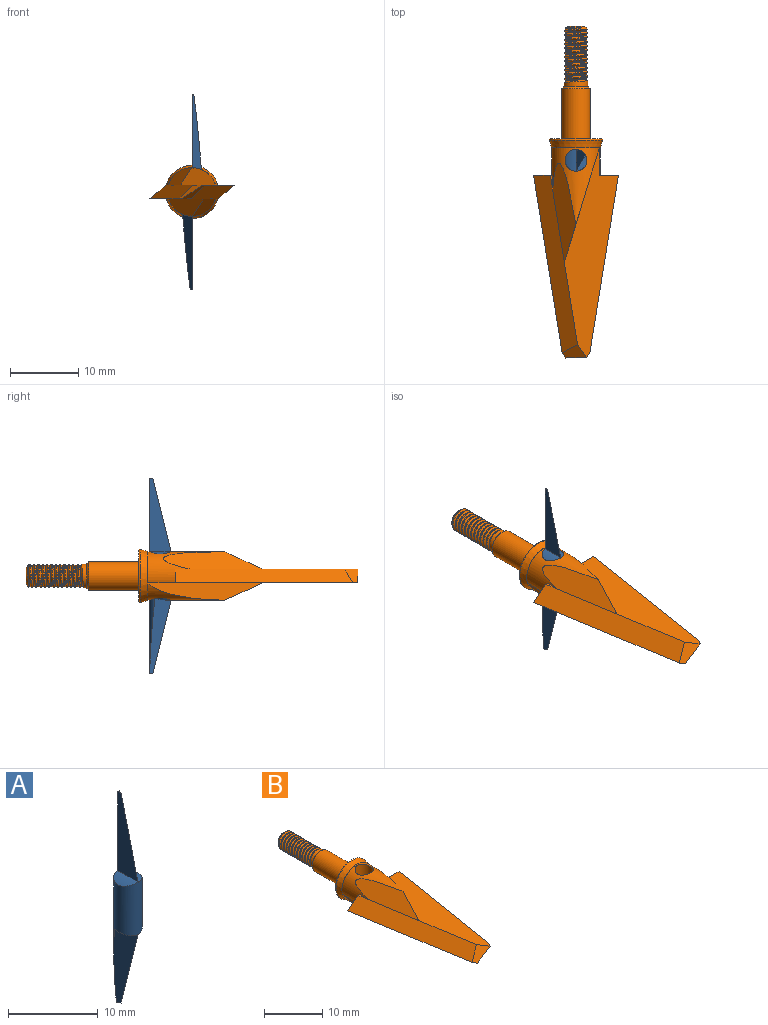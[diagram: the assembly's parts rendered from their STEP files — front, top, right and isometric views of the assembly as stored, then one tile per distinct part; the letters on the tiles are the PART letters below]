
ASSEMBLY  parts=2 mates=1
PART A: 13 faces, bbox 3.3x3.3x28.7 mm
  f0: cylinder r=1.59mm len=28.58mm, axis (0,0,-1), area 87.8mm2, adj f1,f2,f3,f4,f6,f7,f8,f9
  f1: cylinder r=3.56mm len=2.38mm, axis (0,1,0), area 1.6mm2, adj f0,f5,f9,f12
  f2: plane 10.73x3.18mm, normal (-1,0,0), area 19.8mm2, adj f0,f4,f7,f11
  f3: cylinder r=3.56mm len=3.18mm, axis (0,1,0), area 4.1mm2, adj f0,f6
  f4: plane 11.09x3.24mm, normal (0.87,-0.49,0.12), area 19.3mm2, adj f0,f2,f8,f11
  f5: plane 0.07x0.04mm, normal (-0.5,0.86,0.12), area 0mm2, adj f1,f9,f12
  f6: plane 10.73x3.18mm, normal (1,0,0), area 19.8mm2, adj f0,f3,f9,f10
  f7: cylinder r=3.56mm len=3.18mm, axis (0,1,0), area 4.1mm2, adj f0,f2
  f8: cylinder r=3.56mm len=2.38mm, axis (0,1,0), area 1.6mm2, adj f0,f4
  f9: plane 11.03x3.17mm, normal (-0.87,-0.49,-0.12), area 19.3mm2, adj f0,f1,f5,f6,f10,f12
  f10: plane 0.51x0.27mm, normal (0,0,-1), area 0.1mm2, adj f0,f6,f9
  f11: plane 0.51x0.27mm, normal (0,0,1), area 0.1mm2, adj f0,f2,f4
  f12: plane 1.08x0.59mm, normal (0.08,0.11,-0.99), area 0.1mm2, adj f1,f5,f9
PART B: 44 faces, bbox 12.4x48.5x8.4 mm
  f0: cylinder r=2.08mm len=7.37mm, axis (0,-1,0), area 96.4mm2, adj f2,f36
  f1: plane 3.66x3.66mm, normal (0,1,0), area 0.9mm2, adj f2,f3
  f2: cone r=1.83mm half-angle=45deg, axis (0,-1,0), area 4.4mm2, adj f0,f1
  f3: cylinder r=1.75mm len=3.51mm, axis (0,-1,0), area 7.4mm2, adj f1,f4,f18,f19,f21
  f4: cylinder r=1.75mm len=3.51mm, axis (0,-1,0), area 1mm2, adj f3,f5,f19,f21
  f5: cylinder r=1.75mm len=3.51mm, axis (0,-1,0), area 1mm2, adj f4,f6,f19,f21
  f6: cylinder r=1.75mm len=3.51mm, axis (0,-1,0), area 1mm2, adj f5,f7,f19,f21
  f7: cylinder r=1.75mm len=3.51mm, axis (0,-1,0), area 1mm2, adj f6,f8,f19,f21
  f8: cylinder r=1.75mm len=3.51mm, axis (0,-1,0), area 1mm2, adj f7,f9,f19,f21
  f9: cylinder r=1.75mm len=3.51mm, axis (0,-1,0), area 1mm2, adj f8,f10,f19,f21
  f10: cylinder r=1.75mm len=3.51mm, axis (0,-1,0), area 1mm2, adj f9,f11,f19,f21
  f11: cylinder r=1.75mm len=3.51mm, axis (0,-1,0), area 1mm2, adj f10,f12,f19,f21
  f12: cylinder r=1.75mm len=3.51mm, axis (0,-1,0), area 1mm2, adj f11,f13,f19,f21
  f13: cylinder r=1.75mm len=3.51mm, axis (0,-1,0), area 1mm2, adj f12,f14,f19,f21
  f14: cylinder r=1.75mm len=3.51mm, axis (0,-1,0), area 1mm2, adj f13,f15,f19,f21
  f15: cylinder r=1.75mm len=1.33mm, axis (0,-1,0), area 0.1mm2, adj f14,f17,f21
  f16: plane 2.49x2.49mm, normal (0,1,0), area 4.9mm2, adj f17
  f17: cone r=1.24mm half-angle=45deg, axis (0,-1,0), area 4.6mm2, adj f15,f16,f19,f20,f21
  f18: plane 0.55x0.27mm, normal (0,0,-1), area 0.1mm2, adj f3,f19,f20,f21
  f19: bspline ~8.47x4.05mm, area 45.1mm2, adj f3,f4,f5,f6,f7,f8,f9,f10
  f20: cylinder r=1.48mm len=8.16mm, axis (0,1,0), area 20.7mm2, adj f17,f18,f19,f21
  f21: bspline ~8.23x4.05mm, area 41.3mm2, adj f3,f4,f5,f6,f7,f8,f9,f10
  f22: cylinder r=3.56mm len=11.24mm, axis (0,1,0), area 42.9mm2, adj f23,f24,f25,f26,f27,f37,f39
  f23: plane 16.75x5.11mm, normal (0.96,-0.29,0), area 29.3mm2, adj f22,f24,f28
  f24: plane 14.43x3.39mm, normal (-0.7,-0.11,0.71), area 37.1mm2, adj f22,f23,f34
  f25: plane 2.13x0.34mm, normal (0,0,1), area 0.4mm2, adj f22,f26,f34
  f26: plane 2.8x2.03mm, normal (0,1,0), area 3mm2, adj f22,f25,f27,f34
  f27: plane 30.73x7.91mm, normal (0,0,-1), area 114.7mm2, adj f22,f26,f30,f32,f33,f34,f41,f42
  f28: plane 30.73x7.91mm, normal (0,0,1), area 114.7mm2, adj f23,f29,f30,f32,f33,f34,f40
  f29: plane 2.8x2.03mm, normal (0,1,0), area 3mm2, adj f28,f31,f33,f40
  f30: plane 3.55x2.03mm, normal (-0.52,-0.34,0.78), area 5.3mm2, adj f27,f28,f32,f34
  f31: plane 2.13x0.34mm, normal (0,0,-1), area 0.4mm2, adj f29,f33,f40
  f32: plane 3.55x2.03mm, normal (0.52,-0.34,-0.78), area 5.3mm2, adj f27,f28,f30,f33
  f33: plane 25.9x6.43mm, normal (0.63,-0.1,-0.77), area 81mm2, adj f27,f28,f29,f31,f32,f43
  f34: plane 25.9x6.43mm, normal (-0.63,-0.1,0.77), area 81mm2, adj f24,f25,f26,f27,f28,f30
  f35: cone r=3.94mm half-angle=16deg, axis (0,1,0), area 27mm2, adj f37,f38
  f36: plane 7.54x7.54mm, normal (0,1,0), area 31mm2, adj f0,f38
  f37: plane 7.15x7.15mm, normal (0,-1,0), area 0.4mm2, adj f22,f35,f40
  f38: torus R=3.77mm, axis (0,1,0), area 5.7mm2, adj f35,f36
  f39: cylinder r=1.59mm len=6.36mm, axis (0,0,-1), area 63.5mm2, adj f22,f40
  f40: cylinder r=3.56mm len=11.25mm, axis (0,-1,0), area 43mm2, adj f28,f29,f31,f37,f39,f42,f43
  f41: plane 0x0mm, normal (0,-1,0), area 0mm2, adj f27,f42,f43
  f42: plane 16.76x5.11mm, normal (-0.96,-0.29,0), area 29.3mm2, adj f27,f40,f41,f43
  f43: plane 14.45x3.39mm, normal (0.7,-0.11,-0.71), area 37.1mm2, adj f33,f40,f41,f42
PLACE A t=(0,2.21,0)mm
PLACE B at identity fixed
MATE cylindrical B.f39 <-> A.f0  axis (0,0,-1) through (0,2.21,0)mm
